# Revit family: Natre Tilt and turn casement door
name_source: partatom
category: Doors
units: mm (PartAtom-declared; Revit-internal decimal feet)

## family parameters
Always vertical = Yes
Cut with Voids When Loaded = No
Host = Wall
OmniClass Number = 23.30.20.00
OmniClass Title = Windows
Room Calculation Point = Yes
Shared = No

## types (1)
- 948x2118
    Default Sill Height = 0 mm  [stored 0 ft]
    Desire Height = 2118 mm  [stored 6.94882 ft]
    Desire Width = 948 mm  [stored 3.11024 ft]
    Exterior Frame = Default
    Glass = Glass
    Height = 2118 mm  [stored 6.94882 ft]
    Interior Frame = Default
    Joint = 12 mm  [stored 0.0393701 ft]
    Manufacturer = Natre
    Model = GENP FI CD TITU_SC
    Placement in wall = 50 mm  [stored 0.164042 ft]
    Rough Height = 2142 mm  [stored 7.02756 ft]
    Rough Width = 972 mm
    URL = www.natre.no
    Wall Closure = By host
    Wall closure = 150 mm
    Width = 948 mm  [stored 3.11024 ft]

note: [stored X ft] marks values corroborated as IEEE doubles in the binary element streams (Revit-internal decimal feet)

## geometry (parser evidence)
native form markers: Sweep x5
no freeform markers — native parametric forms only
